# Revit family: Air-Curtain_Window-PassThru_PoweredAire_PTW
name_source: partatom
category: Mechanical Equipment
revit_build: Autodesk Revit 2018 (Build: 20170927_1515(x64)
units: mm (PartAtom-declared; Revit-internal decimal feet)

## family parameters
Cut with Voids When Loaded = No
Host = Face
OmniClass Number = 23.75.35.17.21
OmniClass Title = Air Curtains
Part Type = Normal
Room Calculation Point = No
Round Connector Dimension = Use Diameter
Shared = No

## types (2) — shared parameters
Assembly Code = D3090400
Construction Details = http://www.arcat.com
Default Elevation = 0' - 0"
Electrical_Voltage = 120 V
Green Building-LEED = http://www.arcat.com
HVAC_Outlet Velocity = 1700 FPM
HVAC_Outlet Volume = 360 CFM
Keynote = 23 34 33
Manufacturer = Powered Aire, Inc
Manufacturer Fax = 724-588-3371
Manufacturer Website = http://www.poweredaire.com
Max Height = 3' - 6"
Power Rating = 107 W
Product Data = http://www.arcat.com
Revision = R1_2016-08
Sales Information = http://www.poweredaire.com
Sound Pressure = 50 dBA
Specification = http://www.arcat.com
Standards Conformance = ETL  ;  Made in USA
URL = http://www.poweredaire.com
Unit Depth = 0' - 4 1/2"
Unit Height = 0' - 4 15/16"
Unit Width Notes = Other Widths available.
zero-valued in all types: Expected Lifespan (Years), HVAC_Outlet Velocity Uniformity, Maintenance Schedule (Months), Warranty Duration (Years)

## per-type parameters (varying)
| type | Description | Electrical_Amperage | HVAC_Temperature Rise | Heating Element Load | Model | Mounting Width | Nozzle Width | Unit Weight | Unit Width |
| Elec Heat | Powered Aire Electrically Heated PassThru Window Air Curtain - PTW-24E as Specified | 11 A | 11 °F | 1200 W | PTW-24E | 2' - 6 5/16" | 2' - 6 1/4" | 21 | 2' - 7 1/4" |
| Unheated | Powered Aire Unheated PassThru Window Air Curtain - PTW-24 as Specified | 2 A | 0 °F | 0 W | PTW-24 | 2' - 4 5/16" | 2' - 4 1/4" | 13 | 2' - 5 1/4" |

## geometry (parser evidence)
native form markers: Sweep x3
no freeform markers — native parametric forms only
